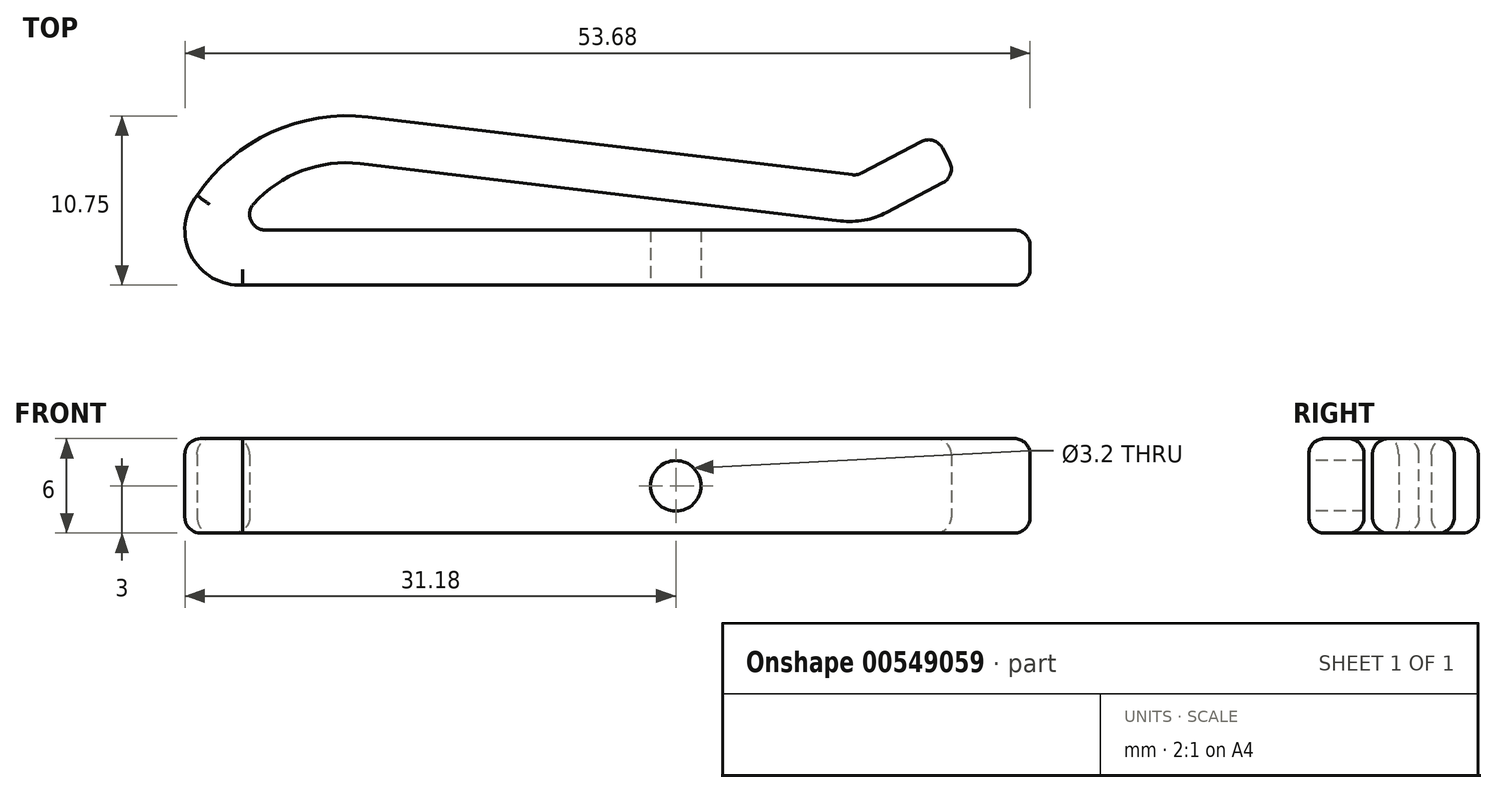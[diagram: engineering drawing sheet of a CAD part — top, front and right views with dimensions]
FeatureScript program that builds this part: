
annotation { "Feature Type Name" : "Feature", "Feature Type Description" : "" }
export const myFeature = defineFeature(function(context is Context, id is Id, definition is map)
    precondition{}
    {
        {
            var Q0;
            Q0=qCreatedBy(makeId("Top.planeOp"),FACE);
            var sketch = newSketch(context, id + "F0", { "sketchPlane" : qUnion([Q0])});
            skLineSegment(sketch, "E0.bottom", {"start": v(1.43, 0) * mm, "end": v(50, 0) * mm});
            skLineSegment(sketch, "E0.top", {"start": v(0, -3.5) * mm, "end": v(50, -3.5) * mm});
            skLineSegment(sketch, "E0.right", {"start": v(50, 0) * mm, "end": v(50, -3.5) * mm});
            skArc(sketch, "E1", {"start": v(7.96, 7.17) * mm, "mid": v(1.83, 6.21) * mm, "end": v(-2.9, 2.2) * mm});
            skArc(sketch, "E2", {"start": v(7.45, 4.21) * mm, "mid": v(3.76, 3.76) * mm, "end": v(0.69, 1.66) * mm});
            skPoint(sketch, "E0.left.start.orphan", {"position": v(0, 0) * mm});
            skArc(sketch, "E3.trimOffspring", {"start": v(-2.9, 2.2) * mm, "mid": v(-3.3, -1.6) * mm, "end": v(0, -3.5) * mm});
            skArc(sketch, "E4", {"start": v(0.69, 1.66) * mm, "mid": v(0.52, 0.59) * mm, "end": v(1.43, 0) * mm});
            skLineSegment(sketch, "E5", {"start": v(7.45, 4.21) * mm, "end": v(39.52, 0.4) * mm});
            skLineSegment(sketch, "E6", {"start": v(7.96, 7.17) * mm, "end": v(39.03, 3.47) * mm});
            skLineSegment(sketch, "E7", {"start": v(39.03, 3.47) * mm, "end": v(43.97, 6.08) * mm});
            skLineSegment(sketch, "E8", {"start": v(43.97, 6.08) * mm, "end": v(45.35, 3.47) * mm});
            skLineSegment(sketch, "E9", {"start": v(45.35, 3.47) * mm, "end": v(39.52, 0.4) * mm});
            skSolve(sketch);
        }
        {
            var Q0;
            Q0=qSketchRegion(id+"F0",true);
            extrude(context, id + "F1", {"entities" : qUnion([Q0]), "depth" : 6 * mm, "offsetDistance" : 25 * mm});
        }
        {
            var Q0;
            Q0=makeQuery(id+"F1.opExtrude","SWEPT_EDGE",EDGE,{"disambiguationData":[OSD([sQuery(id+"F0.wireOp",EDGE,"E5"),sQuery(id+"F0.wireOp",EDGE,"E9")])]});
            fillet(context, id + "F2", {"entities" : qUnion([Q0]), "radius" : 5 * mm, "tangentPropagation" : true, "allowEdgeOverflow" : false});
        }
        {
            var Q0;
            Q0=makeQuery(id+"F1.opExtrude","SWEPT_EDGE",EDGE,{"disambiguationData":[OSD([sQuery(id+"F0.wireOp",EDGE,"E6"),sQuery(id+"F0.wireOp",EDGE,"E7")])]});
            var Q1;
            Q1=makeQuery(id+"F1.opExtrude","SWEPT_EDGE",EDGE,{"disambiguationData":[OSD([sQuery(id+"F0.wireOp",EDGE,"E8"),sQuery(id+"F0.wireOp",EDGE,"E9")])]});
            var Q2;
            Q2=makeQuery(id+"F1.opExtrude","CAP_FACE",FACE,{"disambiguationData":[OSD([sQuery(id+"F0.wireOp",EDGE,"E0.bottom"),sQuery(id+"F0.wireOp",EDGE,"E0.top"),sQuery(id+"F0.wireOp",EDGE,"E0.right"),sQuery(id+"F0.wireOp",EDGE,"E1"),sQuery(id+"F0.wireOp",EDGE,"E2"),sQuery(id+"F0.wireOp",EDGE,"E3.trimOffspring"),sQuery(id+"F0.wireOp",EDGE,"E4"),sQuery(id+"F0.wireOp",EDGE,"E5"),sQuery(id+"F0.wireOp",EDGE,"E6"),sQuery(id+"F0.wireOp",EDGE,"E7"),sQuery(id+"F0.wireOp",EDGE,"E8"),sQuery(id+"F0.wireOp",EDGE,"E9")])],"isStart":false});
            var Q3;
            Q3=makeQuery(id+"F1.opExtrude","CAP_FACE",FACE,{"disambiguationData":[OSD([sQuery(id+"F0.wireOp",EDGE,"E0.bottom"),sQuery(id+"F0.wireOp",EDGE,"E0.top"),sQuery(id+"F0.wireOp",EDGE,"E0.right"),sQuery(id+"F0.wireOp",EDGE,"E1"),sQuery(id+"F0.wireOp",EDGE,"E2"),sQuery(id+"F0.wireOp",EDGE,"E3.trimOffspring"),sQuery(id+"F0.wireOp",EDGE,"E4"),sQuery(id+"F0.wireOp",EDGE,"E5"),sQuery(id+"F0.wireOp",EDGE,"E6"),sQuery(id+"F0.wireOp",EDGE,"E7"),sQuery(id+"F0.wireOp",EDGE,"E8"),sQuery(id+"F0.wireOp",EDGE,"E9")])],"isStart":true});
            var Q4;
            Q4=makeQuery(id+"F1.opExtrude","SWEPT_EDGE",EDGE,{"disambiguationData":[OSD([sQuery(id+"F0.wireOp",EDGE,"E0.bottom"),sQuery(id+"F0.wireOp",EDGE,"E0.right")])]});
            var Q5;
            Q5=makeQuery(id+"F1.opExtrude","SWEPT_EDGE",EDGE,{"disambiguationData":[OSD([sQuery(id+"F0.wireOp",EDGE,"E0.top"),sQuery(id+"F0.wireOp",EDGE,"E0.right")])]});
            fillet(context, id + "F3", {"entities" : qUnion([Q0, Q1, Q2, Q3, Q4, Q5]), "radius" : 1 * mm, "tangentPropagation" : true, "allowEdgeOverflow" : false});
        }
        {
            var Q0;
            Q0=makeQuery(id+"F1.opExtrude","SWEPT_EDGE",EDGE,{"disambiguationData":[OSD([sQuery(id+"F0.wireOp",EDGE,"E7"),sQuery(id+"F0.wireOp",EDGE,"E8")])]});
            fillet(context, id + "F4", {"entities" : qUnion([Q0]), "radius" : 1 * mm, "tangentPropagation" : true, "allowEdgeOverflow" : false});
        }
        {
            var Q0;
            Q0=makeQuery(id+"F1.opExtrude","SWEPT_FACE",FACE,{"disambiguationData":[OSD([sQuery(id+"F0.wireOp",EDGE,"E0.top")])]});
            var sketch = newSketch(context, id + "F5", { "sketchPlane" : qUnion([Q0])});
            skCircle(sketch, "E10", {"center": v(27.5, 3) * mm, "radius": 1.6 * mm});
            skPoint(sketch, "E10.centerSnap0", {"position": v(49, 3) * mm});
            skSolve(sketch);
        }
        {
            var Q0;
            Q0 = qSketchRegion(id + "F5", true);
            extrude(context, id + "F6", {"entities" : qUnion([Q0]), "operationType" : NewBodyOperationType.REMOVE, "oppositeDirection" : true, "depth" : 4 * mm, "offsetDistance" : 25 * mm});
        }
    });
